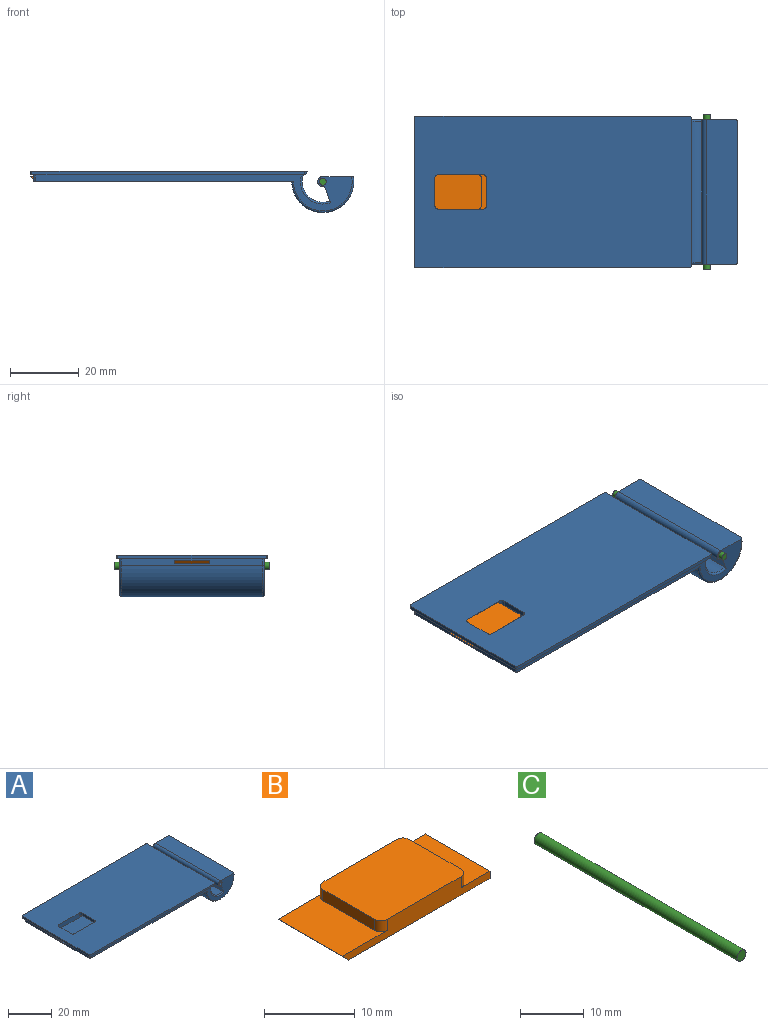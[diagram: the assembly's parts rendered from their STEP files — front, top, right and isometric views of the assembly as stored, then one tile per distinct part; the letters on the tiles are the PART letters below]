
ASSEMBLY  parts=3 mates=2
PART A: 38 faces, bbox 94.7x44x13.2 mm
  f0: plane 80.53x44mm, normal (0,0,1), area 3393.8mm2, adj f13,f14,f15,f16,f17,f18,f19,f20
  f1: plane 10x6mm, normal (0,0,-1), area 50.4mm2, adj f3,f30,f31,f35,f36,f37
  f2: cylinder r=6mm len=41mm, axis (0,1,0), area 555.9mm2, adj f8,f12,f22,f25
  f3: plane 41x2mm, normal (-1,0,0), area 72mm2, adj f1,f4,f12,f21,f24,f28,f30,f31
  f4: plane 75.5x42mm, normal (0,0,-1), area 3150mm2, adj f3,f5,f10,f11,f21,f23,f24,f26
  f5: cylinder r=9mm len=41mm, axis (0,1,0), area 1221mm2, adj f4,f6,f23,f26
  f6: plane 42x8.87mm, normal (0,0,1), area 372.6mm2, adj f5,f7,f10,f11,f23,f26
  f7: cylinder r=1.5mm len=42mm, axis (0,1,0), area 219.9mm2, adj f6,f8,f10,f11
  f8: plane 42x4.7mm, normal (-0.94,0,-0.34), area 189.1mm2, adj f2,f7,f10,f11,f22,f25
  f9: cylinder r=1mm len=42mm, axis (0,1,0), area 263.9mm2, adj f10,f11
  f10: plane 92x10.5mm, normal (0,-1,0), area 240.6mm2, adj f4,f6,f7,f8,f9,f12,f24,f25
  f11: plane 92x10.5mm, normal (0,1,0), area 240.6mm2, adj f4,f6,f7,f8,f9,f12,f21,f22
  f12: plane 80x44mm, normal (0,0,-1), area 229.6mm2, adj f2,f3,f10,f11,f13,f14,f15,f16
  f13: plane 43x1mm, normal (-1,0,0), area 43mm2, adj f0,f12,f17,f19
  f14: cylinder r=5.39mm len=43mm, axis (0,1,0), area 48.7mm2, adj f0,f12,f18,f20
  f15: plane 79.44x1mm, normal (0,-1,0), area 79.2mm2, adj f0,f12,f19,f20
  f16: plane 79.44x1mm, normal (0,1,0), area 79.2mm2, adj f0,f12,f17,f18
  f17: cylinder r=0.5mm len=1mm, axis (0,0,-1), area 0.8mm2, adj f0,f12,f13,f16
  f18: torus R=5.89mm, axis (0,-1,0), area 0.9mm2, adj f0,f12,f14,f16
  f19: cylinder r=0.5mm len=1mm, axis (0,0,1), area 0.8mm2, adj f0,f12,f13,f15
  f20: torus R=5.89mm, axis (0,-1,0), area 0.9mm2, adj f0,f12,f14,f15
  f21: cylinder r=0.5mm len=2mm, axis (0,0,-1), area 1.6mm2, adj f3,f4,f11,f12
  f22: torus R=6.5mm, axis (0,-1,0), area 10.9mm2, adj f2,f8,f11,f12
  f23: torus R=8.5mm, axis (0,-1,0), area 22.9mm2, adj f4,f5,f6,f11
  f24: cylinder r=0.5mm len=2mm, axis (0,0,1), area 1.6mm2, adj f3,f4,f10,f12
  f25: torus R=6.5mm, axis (0,-1,0), area 10.9mm2, adj f2,f8,f10,f12
  f26: torus R=8.5mm, axis (0,-1,0), area 22.9mm2, adj f4,f5,f6,f10
  f27: plane 10x6mm, normal (0,0,-1), area 50.4mm2, adj f29,f30,f31,f32,f33,f34
  f28: plane 25x10mm, normal (0,0,1), area 250mm2, adj f3,f29,f30,f31
  f29: plane 10x1mm, normal (-1,0,0), area 10mm2, adj f27,f28,f30,f31
  f30: plane 25x2.5mm, normal (0,1,0), area 44.5mm2, adj f0,f1,f3,f27,f28,f29,f32,f37
  f31: plane 25x2.5mm, normal (0,-1,0), area 44.5mm2, adj f0,f1,f3,f27,f28,f29,f34,f35
  f32: cylinder r=1mm len=1.5mm, axis (0,0,1), area 2.4mm2, adj f0,f27,f30,f33
  f33: plane 8x1.5mm, normal (-1,0,0), area 12mm2, adj f0,f27,f32,f34
  f34: cylinder r=1mm len=1.5mm, axis (0,0,1), area 2.4mm2, adj f0,f27,f31,f33
  f35: cylinder r=1mm len=1.5mm, axis (0,0,1), area 2.4mm2, adj f0,f1,f31,f36
  f36: plane 8x1.5mm, normal (1,0,0), area 12mm2, adj f0,f1,f35,f37
  f37: cylinder r=1mm len=1.5mm, axis (0,0,1), area 2.4mm2, adj f0,f1,f30,f36
PART B: 14 faces, bbox 23x10x2.5 mm
  f0: plane 10x4.5mm, normal (0,0,1), area 35.4mm2, adj f4,f5,f6,f7,f8,f9
  f1: plane 10x7mm, normal (0,0,1), area 60.4mm2, adj f2,f5,f6,f10,f11,f12
  f2: plane 10x1mm, normal (-0.71,0,-0.71), area 14.1mm2, adj f1,f3,f5,f6
  f3: plane 22x10mm, normal (0,0,-1), area 220mm2, adj f2,f4,f5,f6
  f4: plane 10x1mm, normal (1,0,0), area 10mm2, adj f0,f3,f5,f6
  f5: plane 23x2.5mm, normal (0,-1,0), area 39.8mm2, adj f0,f1,f2,f3,f4,f7,f12,f13
  f6: plane 23x2.5mm, normal (0,1,0), area 39.8mm2, adj f0,f1,f2,f3,f4,f9,f10,f13
  f7: cylinder r=1mm len=1.5mm, axis (0,0,1), area 2.4mm2, adj f0,f5,f8,f13
  f8: plane 8x1.5mm, normal (1,0,0), area 12mm2, adj f0,f7,f9,f13
  f9: cylinder r=1mm len=1.5mm, axis (0,0,1), area 2.4mm2, adj f0,f6,f8,f13
  f10: cylinder r=1mm len=1.5mm, axis (0,0,1), area 2.4mm2, adj f1,f6,f11,f13
  f11: plane 8x1.5mm, normal (-1,0,0), area 12mm2, adj f1,f10,f12,f13
  f12: cylinder r=1mm len=1.5mm, axis (0,0,1), area 2.4mm2, adj f1,f5,f11,f13
  f13: plane 13.5x10mm, normal (0,0,1), area 134.1mm2, adj f5,f6,f7,f8,f9,f10,f11,f12
PART C: 3 faces, bbox 2x45x2 mm
  f0: cylinder r=1mm len=45mm, axis (0,1,0), area 282.7mm2, adj f1,f2
  f1: plane 2x2mm, normal (0,-1,0), area 3.1mm2, adj f0
  f2: plane 2x2mm, normal (0,1,0), area 3.1mm2, adj f0
PLACE A t=(-86.39,92.77,-1.46)mm
PLACE B t=(-86.39,92.77,-1.46)mm
PLACE C t=(-86.39,92.77,-1.46)mm
MATE fastened A.f2 <-> C.f0  axis (0,1,0) through (46.5,113.77,25.54)mm
MATE fastened B.f13 <-> A.f0  axis (0,0,1) through (-25.75,92.77,28.54)mm
